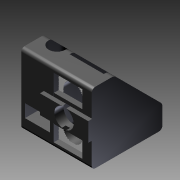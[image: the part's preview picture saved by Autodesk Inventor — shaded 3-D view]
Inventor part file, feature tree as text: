
AUTODESK INVENTOR PART (.ipt)
format: ipt  version: 2016 (Build 200138000, 138)  size: 496,640 bytes
history: native  units: mm
features: other x28, sketch x14, extrude x10, hole x3, revolve x1
ambient origin geometry x8: Origin, YZ Plane, XZ Plane, XY Plane, X Axis, Y Axis, Z Axis, Center Point
bodies: Solid1 (feature_tree)
feature tree (56):
  extrude  "Extrusion1"  Depth=30.0mm TaperAngle=0.0deg
  hole  "Drilling 1"  [1 undecoded]
  hole  "Drilling 2"  [1 undecoded]
  extrude  "Extrusion2"  Depth=17.65mm TaperAngle=0.0deg
  extrude  "Extrusion3"  Depth=8.0mm TaperAngle=0.0deg
  extrude  "Extrusion4"  [1 undecoded]
  revolve  "Revolution1"  [1 undecoded]
  extrude  "Extrusion5"  [1 undecoded]
  extrude  "Extrusion6"  [1 undecoded]
  extrude  "Extrusion7"  [1 undecoded]
  extrude  "Extrusion8"  [1 undecoded]
  extrude  "Extrusion9"  [1 undecoded]
  extrude  "Extrusion10"  [1 undecoded]
  hole  "Drilling 3"  [1 undecoded]
  other  "side_1_XY"
  other  "side_1_YZ"
  other  "side_1_ZX"
  other  "side_1_X"
  other  "side_1_Y"
  other  "side_1_Z"
  other  "side_1_Center"
  other  "side_2a_XY"
  other  "side_2a_YZ"
  other  "side_2a_ZX"
  other  "side_2a_X"
  other  "side_2a_Y"
  other  "side_2a_Z"
  other  "side_2a_Center"
  other  "side_2b_XY"
  other  "side_2b_YZ"
  other  "side_2b_ZX"
  other  "side_2b_X"
  other  "side_2b_Y"
  other  "side_2b_Z"
  other  "side_2b_Center"
  other  "side_2c_XY"
  other  "side_2c_YZ"
  other  "side_2c_ZX"
  other  "side_2c_X"
  other  "side_2c_Y"
  other  "side_2c_Z"
  other  "side_2c_Center"
  sketch  "Skizze_1"  dims[d0=30.0mm d1=0.0mm]
  sketch  "Sketch2"  dims[d9=10.0mm d10=6.0mm d11=4.0mm d12=2.0mm d13=90.0deg d14=13.0mm d15=0.0mm d16=30.0mm d17=0.0mm]
  sketch  "Sketch3"  dims[d18=24.1mm d19=0.0mm d20=30.0mm d21=0.0mm]
  sketch  "Skizze_5"  dims[d29=12.2mm d30=0.0mm d31=8.0mm d32=0.0mm]
  sketch  "Skizze_4"  dims[d22=180.0deg d23=30.0mm d24=0.0mm]
  sketch  "Skizze_6"  dims[d33=12.0mm d34=0.0mm]
  sketch  "Skizze_8"
  sketch  "Skizze_9"
  sketch  "Skizze_10"
  sketch  "Skizze_11"
  sketch  "Skizze_7"  dims[d35=8.2mm d36=6.0mm d37=4.0mm d38=2.0mm d39=90.0deg d40=4.0mm d41=0.0mm]
  sketch  "Sketch_1"  dims[d2=6.647mm d3=12.0mm d4=8.0mm d5=2.0mm d6=15.707963mm d7=12.0mm d8=0.0mm]
  sketch  "Sketch_4"  dims[d25=2.0mm d26=0.0mm d27=17.65mm d28=0.0mm]
  sketch  "Sketch14"
note: 11 required parameter values undecoded (feature->parameter linkage not recoverable at this tier; creation-order binding heuristic only, values carry confidence <= 0.55)
